# Revit family: Wireless_Hub-Lutron-Vive
name_source: partatom
category: Lighting Devices
revit_build: Autodesk Revit 2017 (Build: 20160720_1515(x64)
units: mm (PartAtom-declared; Revit-internal decimal feet)

## family parameters
Cut with Voids When Loaded = No
Host = Face
Maintain Annotation Orientation = No
OmniClass Number = 23.80.30.11
OmniClass Title = Power Supply Devices
Part Type = Normal
Room Calculation Point = No
Round Connector Dimension = Use Diameter
Shared = No

## types (5) — shared parameters
Current = 0 A
Default Elevation = 0' - 0"
Hub Diameter = 0' - 6 13/16"
Hub Height = 0' - 0 3/16"
Hub Material = Plastic - Lutron - White
Hub Radius = 0' - 3 13/32"
Instruction Sheet Link = http://www.lutron.com
Manufacturer = Lutron Electronics Co., Inc
Manufacturer Fax Number = 610-282-1243
Maximum Operating Temperature = 104 °F
Minimum Operating Temperature = 32 °F
Performance URL = http://www.lutron.com
Product Documentation Link = http://www.lutron.com
Product Name = Vive Wireless Hub
Product Page URL = http://www.lutron.com
URL = http://www.lutron.com
Version = 2017 - v1.0b
Video Link = https://www.youtube.com
Voltage = 24 V
Warranty URL = http://www.lutron.com
zero-valued in all types: Cost

## per-type parameters (varying)
| type | Description | Flush Mount Visibility | Hub Label | Model | Series |
| HJS-1-FM | Vive™ hub without BACnet | 0 | 1 | HJS-1-FM | Vive Wireless Hub e™ hub, flush-mount adapter and power supply |
| HJS-1-SM | Vive™ hub without BACnet | 1 | 1 | HJS-1-SM | VivVive Wireless Hub e™ hub, flush-mount adapter andpower supply |
| HJS-2-FM | Premium Vive™ hub with BACnet | 0 | 2 | HJS-2-FM | VivVive Wireless Hub e™ hub, flush-mount adapter andpower supply |
| HJS-2-SM | Premium Vive™ hub with BACnet | 1 | 2 | HJS-2-SM | VivVive Wireless Hub e™ hub, flush-mount adapter andpower supply |
| Power Supply | Premium Vive™ hub with BACnet | 1 | 2 | HJS-2-SM | VivVive Wireless Hub e™ hub, flush-mount adapter andpower supply |

## geometry (parser evidence)
native form markers: Sweep x3
no freeform markers — native parametric forms only
